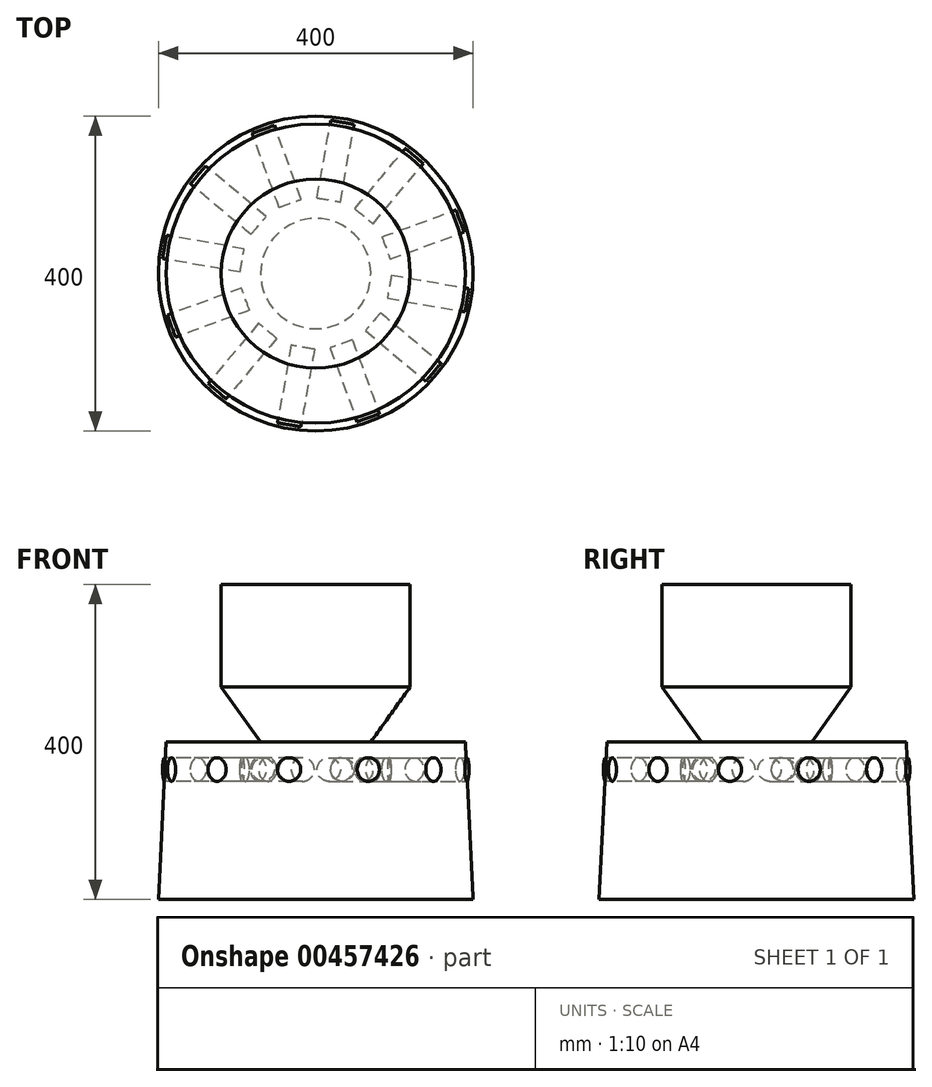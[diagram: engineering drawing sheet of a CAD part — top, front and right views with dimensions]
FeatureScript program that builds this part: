
annotation { "Feature Type Name" : "Feature", "Feature Type Description" : "" }
export const myFeature = defineFeature(function(context is Context, id is Id, definition is map)
    precondition{}
    {
        {
            var Q0;
            Q0=qCreatedBy(makeId("Front.planeOp"),FACE);
            var sketch = newSketch(context, id + "F0", { "sketchPlane" : qUnion([Q0])});
            skLineSegment(sketch, "E0", {"start": v(0, 0) * mm, "end": v(200, 0) * mm});
            skLineSegment(sketch, "E1", {"start": v(200, 0) * mm, "end": v(190, 200) * mm});
            skLineSegment(sketch, "E2", {"start": v(190, 200) * mm, "end": v(0, 200) * mm});
            skLineSegment(sketch, "E3", {"start": v(0, 200) * mm, "end": v(0, 0) * mm});
            skLineSegment(sketch, "E4", {"start": v(0, 122.57) * mm, "end": v(0, -55.9) * mm, "construction": true});
            skSolve(sketch);
        }
        {
            var Q0;
            Q0=makeQuery(id+"F0.imprint","IMPRINT",FACE,{"disambiguationData":[TD([[makeQuery(id+"F0.imprint","IMPRINT",EDGE,{"derivedFrom":sQuery(id+"F0.wireOp",EDGE,"E0")}),1.0]])]});
            var Q1;
            Q1=sQuery(id+"F0.wireOp",EDGE,"E4");
            revolve(context, id + "F1", {"entities" : qUnion([Q0]), "axis" : qUnion([Q1]), "revolveType" : RevolveType.FULL});
        }
        {
            var Q0;
            Q0=qCreatedBy(makeId("Front.planeOp"),FACE);
            var sketch = newSketch(context, id + "F2", { "sketchPlane" : qUnion([Q0])});
            skLineSegment(sketch, "E5", {"start": v(120, 270) * mm, "end": v(120, 400) * mm});
            skLineSegment(sketch, "E6", {"start": v(120, 400) * mm, "end": v(0, 400) * mm});
            skLineSegment(sketch, "E7", {"start": v(0, 400) * mm, "end": v(0, 199.42) * mm});
            skPoint(sketch, "E8.orphan", {"position": v(0, 200) * mm});
            skPoint(sketch, "E9.0.start.orphan", {"position": v(190, 200) * mm});
            skLineSegment(sketch, "E10.0", {"start": v(0, 200) * mm, "end": v(70, 200) * mm});
            skPoint(sketch, "E11.orphan", {"position": v(-190, 200) * mm});
            skLineSegment(sketch, "E12", {"start": v(70, 200) * mm, "end": v(120, 270) * mm});
            skSolve(sketch);
        }
        {
            var Q0;
            Q0=makeQuery(id+"F2.imprint","IMPRINT",FACE,{"disambiguationData":[TD([[makeQuery(id+"F2.imprint","IMPRINT",EDGE,{"derivedFrom":sQuery(id+"F2.wireOp",EDGE,"E5")}),1.0]])]});
            var Q1;
            Q1=sQuery(id+"F0.wireOp",EDGE,"E4");
            revolve(context, id + "F3", {"operationType" : NewBodyOperationType.ADD, "entities" : qUnion([Q0]), "axis" : qUnion([Q1]), "revolveType" : RevolveType.FULL});
        }
        {
            var Q0;
            Q0=makeQuery(id+"F1.opRevolve","SWEPT_FACE",FACE,{"disambiguationData":[OSD([sQuery(id+"F0.wireOp",EDGE,"E2")])]});
            cPlane(context, id + "F4", {"entities" : qUnion([Q0]), "cplaneType" : CPlaneType.OFFSET, "offset" : 35 * mm, "oppositeDirection" : true, "width" : 150 * mm, "height" : 150 * mm});
        }
        {
            var Q0;
            Q0=qCreatedBy(id+"F4.planeOp",FACE);
            var sketch = newSketch(context, id + "F5", { "sketchPlane" : qUnion([Q0])});
            skCircle(sketch, "E13", {"center": v(0, 0) * mm, "radius": 195 * mm});
            skLineSegment(sketch, "E14", {"start": v(0, 0) * mm, "end": v(183.24, 66.7) * mm});
            skPoint(sketch, "E15", {"position": v(183.24, 66.7) * mm});
            skPoint(sketch, "E16", {"position": v(108.06, 39.33) * mm});
            skSolve(sketch);
        }
        {
            var Q0;
            Q0=sQuery(id+"F5.wireOp",VERTEX,"E15");
            var Q1;
            Q1=sQuery(id+"F5.wireOp",EDGE,"E14");
            cPlane(context, id + "F6", {"entities" : qUnion([Q0, Q1]), "cplaneType" : CPlaneType.LINE_POINT, "offset" : 25 * mm, "width" : 150 * mm, "height" : 150 * mm});
        }
        {
            var Q0;
            Q0=qCreatedBy(id+"F6.planeOp",FACE);
            var sketch = newSketch(context, id + "F7", { "sketchPlane" : qUnion([Q0])});
            skCircle(sketch, "E17", {"center": v(0, 165) * mm, "radius": 15 * mm});
            skSolve(sketch);
        }
        {
            var Q0;
            Q0=makeQuery(id+"F7.imprint","IMPRINT",FACE,{"disambiguationData":[TD([[makeQuery(id+"F7.imprint","IMPRINT",EDGE,{"derivedFrom":sQuery(id+"F7.wireOp",EDGE,"E17")}),1.0]])]});
            extrude(context, id + "F8", {"entities" : qUnion([Q0]), "oppositeDirection" : true, "depth" : 100 * mm});
        }
        {
            var Q0;
            Q0=makeQuery(id+"F8.opExtrude","SWEPT_BODY",BODY,{"disambiguationData":[OSD([sQuery(id+"F7.wireOp",EDGE,"E17")])]});
            var Q1;
            Q1=sQuery(id+"F0.wireOp",EDGE,"E3");
            circularPattern(context, id + "F9", {"entities" : qUnion([Q0]), "axis" : qUnion([Q1]), "angle" : 360 * degree, "instanceCount" : 12, "equalSpace" : true});
        }
    });
